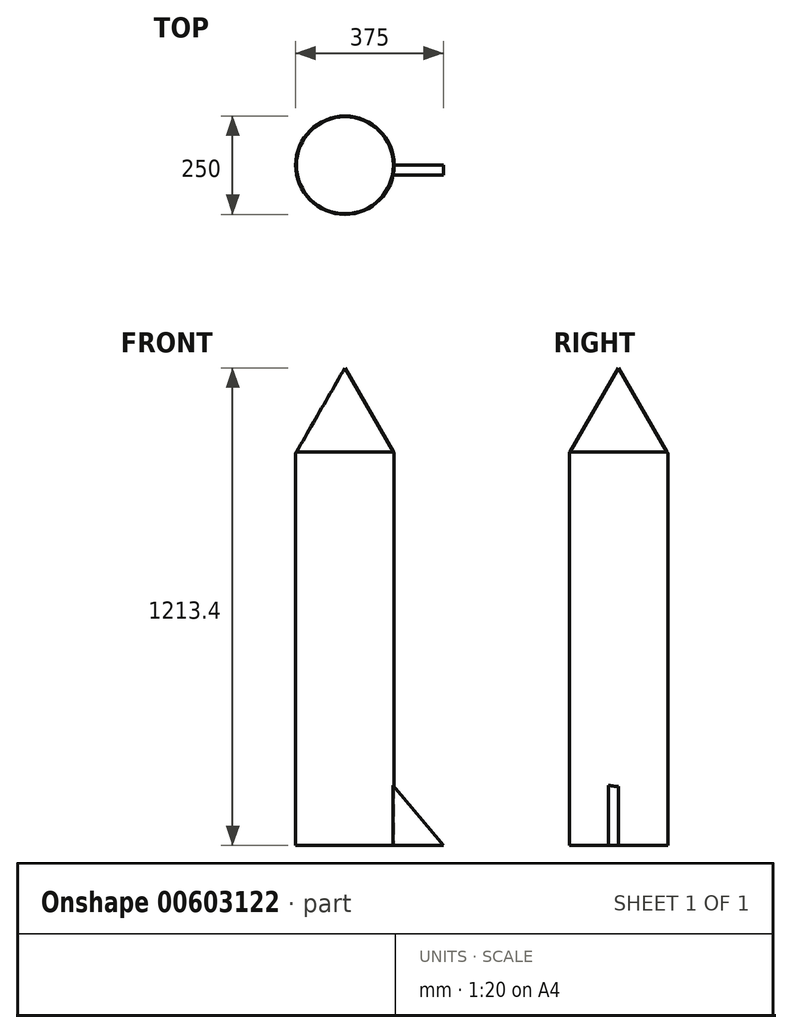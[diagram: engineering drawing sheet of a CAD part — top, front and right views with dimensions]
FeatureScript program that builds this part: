
annotation { "Feature Type Name" : "Feature", "Feature Type Description" : "" }
export const myFeature = defineFeature(function(context is Context, id is Id, definition is map)
    precondition{}
    {
        {
            var Q0;
            Q0=qCreatedBy(makeId("Top.planeOp"),FACE);
            var sketch = newSketch(context, id + "F0", { "sketchPlane" : qUnion([Q0])});
            skCircle(sketch, "E0", {"center": v(0, 0) * mm, "radius": 125 * mm});
            skSolve(sketch);
        }
        {
            var Q0;
            Q0=makeQuery(id+"F0.imprint","IMPRINT",FACE,{"disambiguationData":[TD([[makeQuery(id+"F0.imprint","IMPRINT",EDGE,{"derivedFrom":sQuery(id+"F0.wireOp",EDGE,"E0")}),1.0]])]});
            extrude(context, id + "F1", {"entities" : qUnion([Q0]), "depth" : 1000 * mm, "offsetDistance" : 25 * mm});
        }
        {
            var Q0;
            Q0=qCreatedBy(makeId("Front.planeOp"),FACE);
            var sketch = newSketch(context, id + "F2", { "sketchPlane" : qUnion([Q0])});
            skLineSegment(sketch, "E1", {"start": v(0, 998.61) * mm, "end": v(0, 1213.4) * mm});
            skLineSegment(sketch, "E2", {"start": v(0, 1213.4) * mm, "end": v(-124.55, 997.65) * mm});
            skLineSegment(sketch, "E3", {"start": v(0, 998.61) * mm, "end": v(-124.55, 997.65) * mm});
            skSolve(sketch);
        }
        {
            var Q0;
            Q0 = qSketchRegion(id + "F2", true);
            var Q1;
            Q1=sQuery(id+"F2.wireOp",EDGE,"E1");
            revolve(context, id + "F3", {"operationType" : NewBodyOperationType.ADD, "entities" : qUnion([Q0]), "axis" : qUnion([Q1]), "revolveType" : RevolveType.FULL});
        }
        {
            var Q0;
            Q0=makeQuery(id+"F1.opExtrude","CAP_EDGE",EDGE,{"disambiguationData":[OSD([sQuery(id+"F0.wireOp",EDGE,"E0")])],"isStart":false});
            fillet(context, id + "F4", {"entities" : qUnion([Q0]), "radius" : 5 * mm, "tangentPropagation" : true, "allowEdgeOverflow" : false});
        }
        {
            var Q0;
            Q0=qCreatedBy(makeId("Front.planeOp"),FACE);
            var sketch = newSketch(context, id + "F5", { "sketchPlane" : qUnion([Q0])});
            skLineSegment(sketch, "E4", {"start": v(0, 0) * mm, "end": v(0, 300) * mm});
            skLineSegment(sketch, "E5", {"start": v(0, 0) * mm, "end": v(250, 0) * mm});
            skLineSegment(sketch, "E6", {"start": v(0, 300) * mm, "end": v(250, 0) * mm});
            skSolve(sketch);
        }
        {
            var Q0;
            Q0 = qSketchRegion(id + "F5", true);
            extrude(context, id + "F6", {"entities" : qUnion([Q0]), "operationType" : NewBodyOperationType.ADD, "depth" : 25 * mm, "offsetDistance" : 25 * mm});
        }
    });
